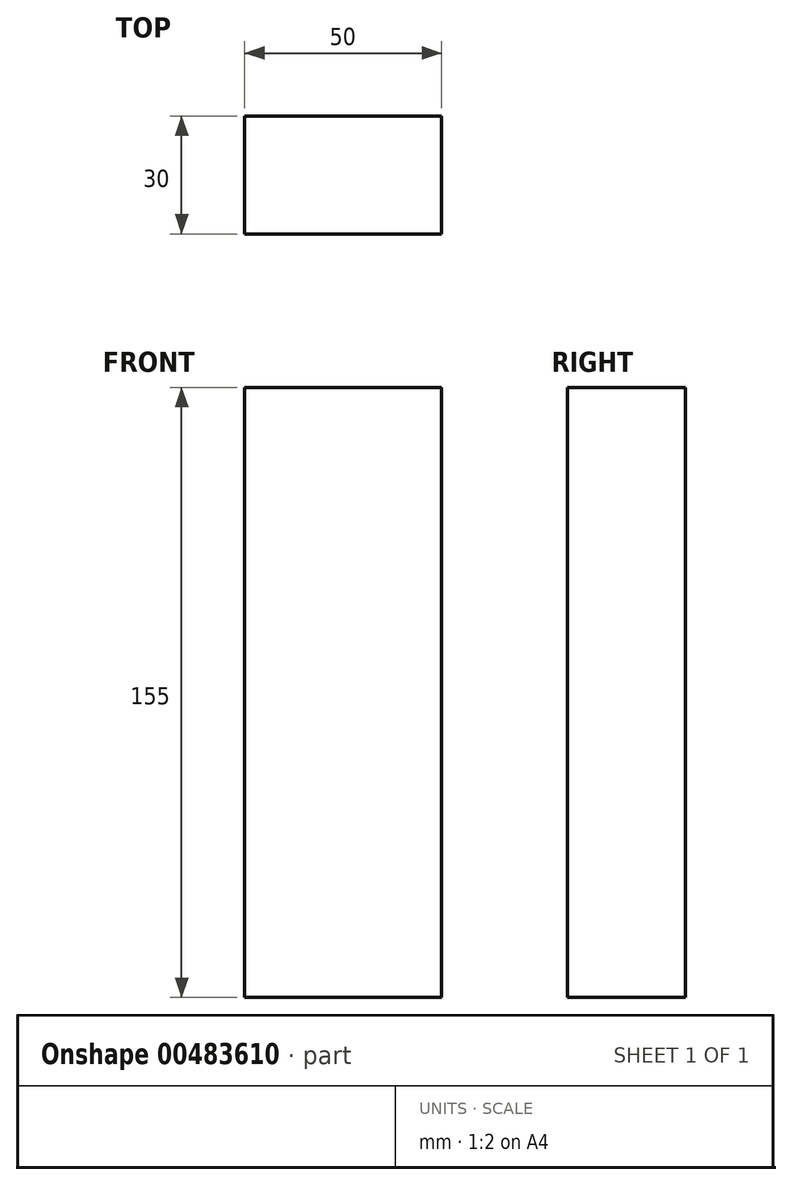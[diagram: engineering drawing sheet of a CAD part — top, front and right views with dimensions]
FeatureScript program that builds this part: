
annotation { "Feature Type Name" : "Feature", "Feature Type Description" : "" }
export const myFeature = defineFeature(function(context is Context, id is Id, definition is map)
    precondition{}
    {
        {
            var Q0;
            Q0=qCreatedBy(makeId("Top.planeOp"),FACE);
            var sketch = newSketch(context, id + "F0", { "sketchPlane" : qUnion([Q0])});
            skLineSegment(sketch, "E0.bottom", {"start": v(25, 15) * mm, "end": v(-25, 15) * mm});
            skLineSegment(sketch, "E0.top", {"start": v(25, -15) * mm, "end": v(-25, -15) * mm});
            skLineSegment(sketch, "E0.left", {"start": v(25, 15) * mm, "end": v(25, -15) * mm});
            skLineSegment(sketch, "E0.right", {"start": v(-25, 15) * mm, "end": v(-25, -15) * mm});
            skPoint(sketch, "E0.middle", {"position": v(0, 0) * mm});
            skSolve(sketch);
        }
        {
            var Q0;
            Q0=makeQuery(id+"F0.imprint","IMPRINT",FACE,{"disambiguationData":[TD([[makeQuery(id+"F0.imprint","IMPRINT",EDGE,{"derivedFrom":sQuery(id+"F0.wireOp",EDGE,"E0.bottom")}),1.0]])]});
            extrude(context, id + "F1", {"entities" : qUnion([Q0]), "depth" : 155 * mm});
        }
    });
